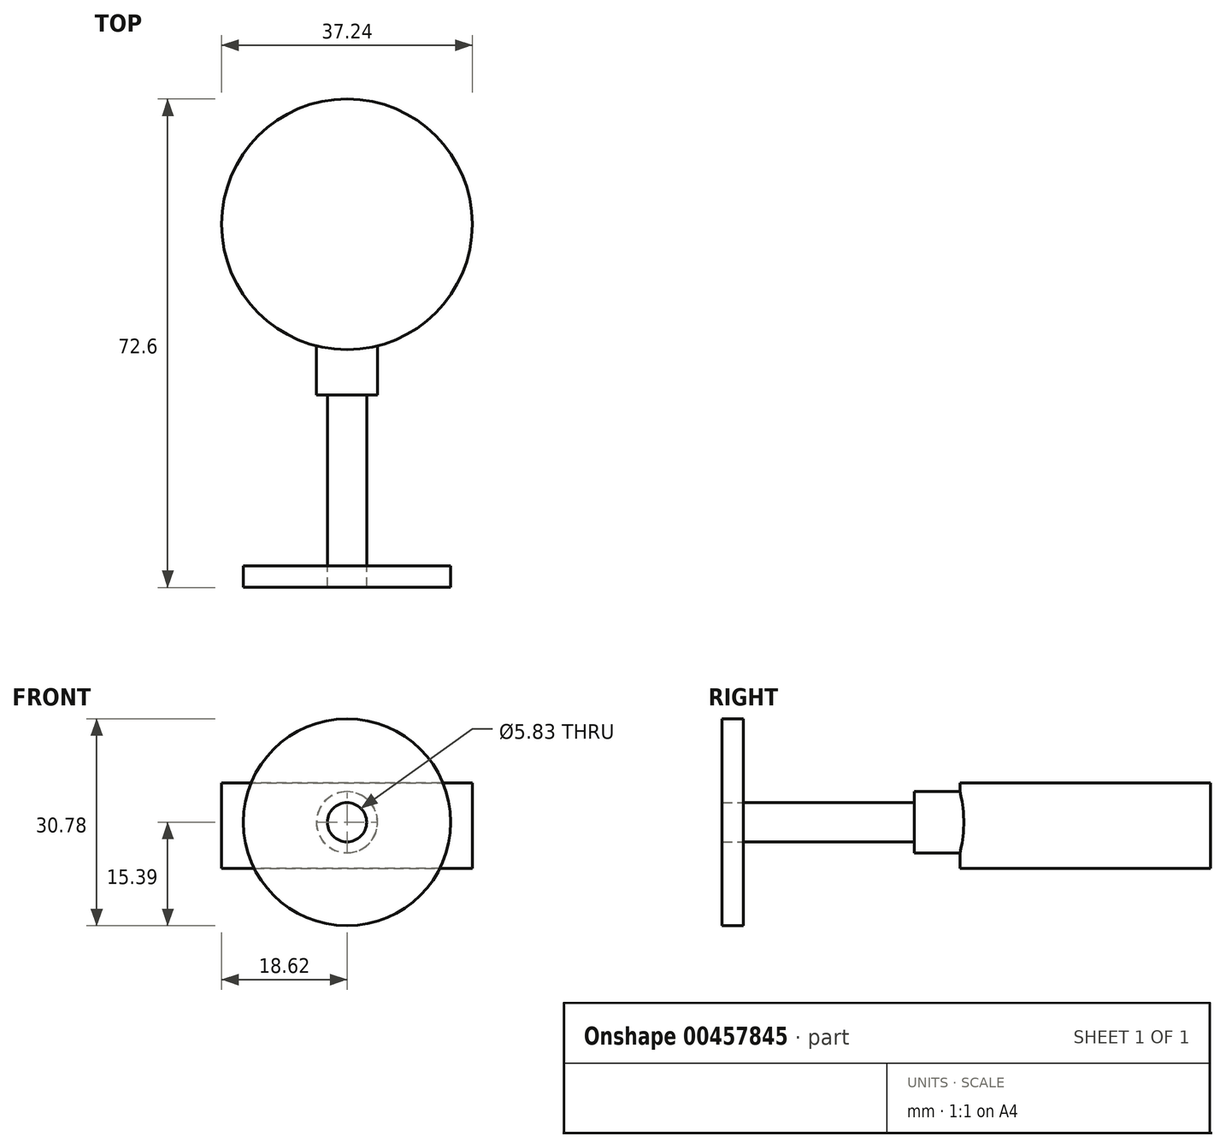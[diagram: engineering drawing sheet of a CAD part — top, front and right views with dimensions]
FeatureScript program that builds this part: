
annotation { "Feature Type Name" : "Feature", "Feature Type Description" : "" }
export const myFeature = defineFeature(function(context is Context, id is Id, definition is map)
    precondition{}
    {
        {
            var Q0;
            Q0=qCreatedBy(makeId("Top.planeOp"),FACE);
            var sketch = newSketch(context, id + "F0", { "sketchPlane" : qUnion([Q0])});
            skCircle(sketch, "E0", {"center": v(0, 0) * mm, "radius": 18.62 * mm});
            skSolve(sketch);
        }
        {
            var Q0;
            Q0=makeQuery(id+"F0.imprint","IMPRINT",FACE,{"disambiguationData":[TD([[makeQuery(id+"F0.imprint","IMPRINT",EDGE,{"derivedFrom":sQuery(id+"F0.wireOp",EDGE,"E0")}),1.0]])]});
            extrude(context, id + "F1", {"entities" : qUnion([Q0]), "depth" : 12.7 * mm});
        }
        {
            var Q0;
            Q0=qCreatedBy(makeId("Front.planeOp"),FACE);
            var sketch = newSketch(context, id + "F2", { "sketchPlane" : qUnion([Q0])});
            skCircle(sketch, "E1", {"center": v(0, 6.85) * mm, "radius": 4.55 * mm});
            skSolve(sketch);
        }
        {
            var Q0;
            Q0 = qSketchRegion(id + "F2", true);
            extrude(context, id + "F3", {"entities" : qUnion([Q0]), "operationType" : NewBodyOperationType.ADD, "depth" : 25.4 * mm});
        }
        {
            var Q0;
            Q0=makeQuery(id+"F3.opExtrude","CAP_FACE",FACE,{"disambiguationData":[OSD([sQuery(id+"F2.wireOp",EDGE,"E1")])],"isStart":false});
            var sketch = newSketch(context, id + "F4", { "sketchPlane" : qUnion([Q0])});
            skCircle(sketch, "E2", {"center": v(0, 6.85) * mm, "radius": 2.91 * mm});
            skSolve(sketch);
        }
        {
            var Q0;
            Q0 = qSketchRegion(id + "F4", true);
            extrude(context, id + "F5", {"entities" : qUnion([Q0]), "operationType" : NewBodyOperationType.ADD, "depth" : 25.4 * mm});
        }
        {
            var Q0;
            Q0=makeQuery(id+"F5.opExtrude","CAP_FACE",FACE,{"disambiguationData":[OSD([sQuery(id+"F4.wireOp",EDGE,"E2")])],"isStart":false});
            var sketch = newSketch(context, id + "F6", { "sketchPlane" : qUnion([Q0])});
            skCircle(sketch, "E3", {"center": v(0, 6.85) * mm, "radius": 15.4 * mm});
            skSolve(sketch);
        }
        {
            var Q0;
            Q0=makeQuery(id+"F6.imprint","IMPRINT",FACE,{"disambiguationData":[TD([[makeQuery(id+"F6.imprint","IMPRINT",EDGE,{"derivedFrom":sQuery(id+"F6.wireOp",EDGE,"E3")}),1.0]])]});
            extrude(context, id + "F7", {"entities" : qUnion([Q0]), "depth" : 3.17 * mm});
        }
    });
